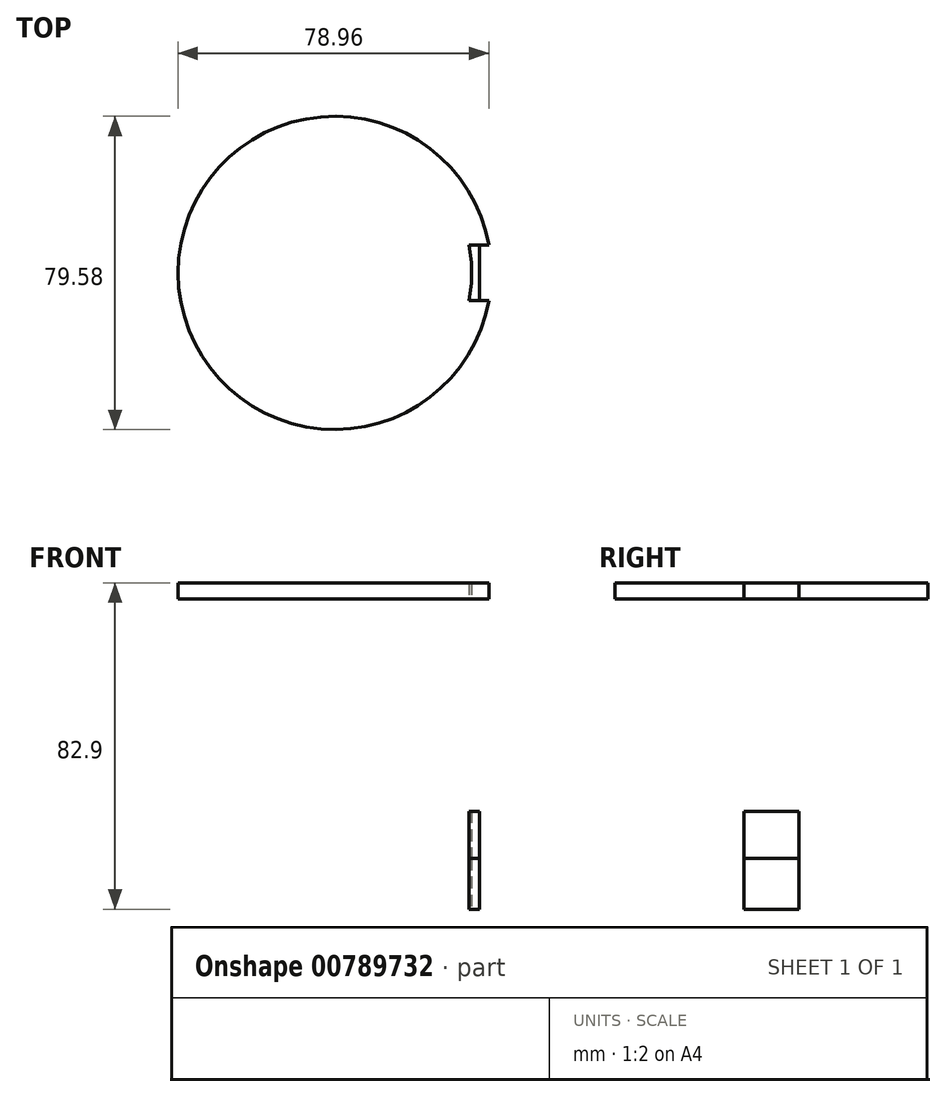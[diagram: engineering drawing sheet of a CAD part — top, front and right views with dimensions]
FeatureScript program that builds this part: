
annotation { "Feature Type Name" : "Feature", "Feature Type Description" : "" }
export const myFeature = defineFeature(function(context is Context, id is Id, definition is map)
    precondition{}
    {
        {
            var Q0;
            Q0=qCreatedBy(makeId("Top.planeOp"),FACE);
            var sketch = newSketch(context, id + "F0", { "sketchPlane" : qUnion([Q0])});
            skCircle(sketch, "E0", {"center": v(0, 0) * mm, "radius": 39.79 * mm});
            skCircle(sketch, "E1", {"center": v(0, 0) * mm, "radius": 34.79 * mm});
            skLineSegment(sketch, "E2.bottom", {"start": v(21, 7) * mm, "end": v(25, 7) * mm});
            skLineSegment(sketch, "E2.top", {"start": v(21, 4) * mm, "end": v(25, 4) * mm});
            skLineSegment(sketch, "E2.left", {"start": v(21, 7) * mm, "end": v(21, 4) * mm});
            skLineSegment(sketch, "E2.right", {"start": v(25, 7) * mm, "end": v(25, 4) * mm});
            skLineSegment(sketch, "E3.MirrorCS", {"start": v(25, -7) * mm, "end": v(25, -4) * mm});
            skLineSegment(sketch, "E4.MirrorCS", {"start": v(21, -4) * mm, "end": v(25, -4) * mm});
            skLineSegment(sketch, "E5.MirrorCS", {"start": v(21, -7) * mm, "end": v(25, -7) * mm});
            skLineSegment(sketch, "E6.MirrorCS", {"start": v(21, -7) * mm, "end": v(21, -4) * mm});
            skLineSegment(sketch, "E7.bottom", {"start": v(21, 7) * mm, "end": v(39.47, 7) * mm});
            skLineSegment(sketch, "E7.top", {"start": v(21, 5) * mm, "end": v(39.47, 5) * mm});
            skLineSegment(sketch, "E7.left", {"start": v(21, 7) * mm, "end": v(21, 5) * mm});
            skLineSegment(sketch, "E7.right", {"start": v(39.47, 7) * mm, "end": v(39.47, 5) * mm});
            skLineSegment(sketch, "E8.bottom", {"start": v(21, -4) * mm, "end": v(39.47, -4) * mm});
            skLineSegment(sketch, "E8.top", {"start": v(21, -7) * mm, "end": v(39.47, -7) * mm});
            skLineSegment(sketch, "E8.left", {"start": v(21, -4) * mm, "end": v(21, -7) * mm});
            skLineSegment(sketch, "E8.right", {"start": v(39.47, -4) * mm, "end": v(39.47, -7) * mm});
            skLineSegment(sketch, "E9.left", {"start": v(21, 7) * mm, "end": v(21, -7) * mm});
            skLineSegment(sketch, "E9.right", {"start": v(25, 7) * mm, "end": v(25, -7) * mm});
            skSolve(sketch);
        }
        {
            var Q0;
            {var subQ3=sQuery(id+"F0.wireOp",EDGE,"E7.bottom");var subQ5=sQuery(id+"F0.wireOp",EDGE,"E1");var subQ6=makeQuery(id+"F0.imprint","INTERSECT",VERTEX,{"derivedFrom":[subQ5,subQ3]});Q0=makeQuery(id+"F0.imprint","IMPRINT",FACE,{"disambiguationData":[TD([[makeQuery(id+"F0.imprint","IMPRINT",EDGE,{"disambiguationData":[TD([[subQ6,1.0]])],"derivedFrom":subQ5}),-1.0]])]});}
            var Q1;
            {var subQ0=sQuery(id+"F0.wireOp",EDGE,"E7.top");var subQ5=sQuery(id+"F0.wireOp",EDGE,"E1");var subQ6=makeQuery(id+"F0.imprint","INTERSECT",VERTEX,{"derivedFrom":[subQ5,subQ0]});Q1=makeQuery(id+"F0.imprint","IMPRINT",FACE,{"disambiguationData":[TD([[makeQuery(id+"F0.imprint","IMPRINT",EDGE,{"disambiguationData":[TD([[subQ6,1.0]])],"derivedFrom":subQ5}),-1.0]])]});}
            var Q2;
            {var subQ3=sQuery(id+"F0.wireOp",EDGE,"E8.top");var subQ5=sQuery(id+"F0.wireOp",EDGE,"E1");var subQ6=makeQuery(id+"F0.imprint","INTERSECT",VERTEX,{"derivedFrom":[subQ5,subQ3]});Q2=makeQuery(id+"F0.imprint","IMPRINT",FACE,{"disambiguationData":[TD([[makeQuery(id+"F0.imprint","IMPRINT",EDGE,{"disambiguationData":[TD([[subQ6,-1.0]])],"derivedFrom":subQ5}),-1.0]])]});}
            extrude(context, id + "F1", {"entities" : qUnion([Q0, Q1, Q2]), "depth" : 160 * mm, "offsetDistance" : 25 * mm, "hasSecondDirection" : true, "secondDirectionOppositeDirection" : false, "secondDirectionDepth" : 90 * mm});
        }
        {
            var Q0;
            Q0=qCreatedBy(makeId("Top.planeOp"),FACE);
            var sketch = newSketch(context, id + "F2", { "sketchPlane" : qUnion([Q0])});
            skLineSegment(sketch, "E10.bottom", {"start": v(33.13, 9) * mm, "end": v(36.74, 9) * mm});
            skLineSegment(sketch, "E10.top", {"start": v(33.13, -11.23) * mm, "end": v(36.74, -11.23) * mm});
            skLineSegment(sketch, "E10.left", {"start": v(33.13, 9) * mm, "end": v(33.13, -11.23) * mm});
            skLineSegment(sketch, "E10.right", {"start": v(36.74, 9) * mm, "end": v(36.74, -11.23) * mm});
            skSolve(sketch);
        }
        {
            var Q0;
            {var subQ0=sQuery(id+"F0.wireOp",EDGE,"E8.top");var subQ1=sQuery(id+"F0.wireOp",EDGE,"E0");var subQ2=makeQuery(id+"F0.imprint","INTERSECT",VERTEX,{"derivedFrom":[subQ1,subQ0]});Q0=makeQuery(id+"F0.imprint","IMPRINT",FACE,{"disambiguationData":[TD([[makeQuery(id+"F0.imprint","IMPRINT",EDGE,{"disambiguationData":[TD([[subQ2,-1.0]])],"derivedFrom":subQ1}),1.0]])]});}
            var Q1;
            {var subQ0=sQuery(id+"F0.wireOp",EDGE,"E7.top");var subQ3=sQuery(id+"F0.wireOp",EDGE,"E1");var subQ4=makeQuery(id+"F0.imprint","INTERSECT",VERTEX,{"derivedFrom":[subQ3,subQ0]});Q1=makeQuery(id+"F0.imprint","IMPRINT",FACE,{"disambiguationData":[TD([[makeQuery(id+"F0.imprint","IMPRINT",EDGE,{"disambiguationData":[TD([[subQ4,1.0]])],"derivedFrom":subQ3}),-1.0]])]});}
            var Q2;
            {var subQ3=sQuery(id+"F0.wireOp",EDGE,"E7.bottom");var subQ5=sQuery(id+"F0.wireOp",EDGE,"E1");var subQ6=makeQuery(id+"F0.imprint","INTERSECT",VERTEX,{"derivedFrom":[subQ5,subQ3]});Q2=makeQuery(id+"F0.imprint","IMPRINT",FACE,{"disambiguationData":[TD([[makeQuery(id+"F0.imprint","IMPRINT",EDGE,{"disambiguationData":[TD([[subQ6,1.0]])],"derivedFrom":subQ5}),-1.0]])]});}
            extrude(context, id + "F3", {"entities" : qUnion([Q0, Q1, Q2]), "depth" : 90 * mm, "offsetDistance" : 25 * mm});
        }
        {
            var Q0;
            Q0=qSketchRegion(id+"F2",true);
            extrude(context, id + "F4", {"entities" : qUnion([Q0]), "operationType" : NewBodyOperationType.INTERSECT, "depth" : 102 * mm, "offsetDistance" : 25 * mm, "hasSecondDirection" : true, "secondDirectionOppositeDirection" : false, "secondDirectionDepth" : 77.1 * mm});
        }
        {
            var Q0;
            {var subQ0=sQuery(id+"F0.wireOp",EDGE,"E7.bottom");var subQ1=sQuery(id+"F0.wireOp",EDGE,"E0");var subQ2=makeQuery(id+"F0.imprint","INTERSECT",VERTEX,{"derivedFrom":[subQ1,subQ0]});Q0=makeQuery(id+"F0.imprint","IMPRINT",FACE,{"disambiguationData":[TD([[makeQuery(id+"F0.imprint","IMPRINT",EDGE,{"disambiguationData":[TD([[subQ2,-1.0]])],"derivedFrom":subQ1}),1.0]])]});}
            var Q1;
            {var subQ0=sQuery(id+"F0.wireOp",EDGE,"E2.bottom");Q1=makeQuery(id+"F0.imprint","IMPRINT",FACE,{"disambiguationData":[TD([[makeQuery(id+"F0.imprint","IMPRINT",EDGE,{"derivedFrom":subQ0}),1.0]])]});}
            var Q2;
            {var subQ2=sQuery(id+"F0.wireOp",EDGE,"E7.top");var subQ4=sQuery(id+"F0.wireOp",EDGE,"E1");var subQ5=makeQuery(id+"F0.imprint","INTERSECT",VERTEX,{"derivedFrom":[subQ4,subQ2]});Q2=makeQuery(id+"F0.imprint","IMPRINT",FACE,{"disambiguationData":[TD([[makeQuery(id+"F0.imprint","IMPRINT",EDGE,{"disambiguationData":[TD([[subQ5,1.0]])],"derivedFrom":subQ4}),1.0]])]});}
            var Q3;
            {var subQ0=sQuery(id+"F0.wireOp",EDGE,"E2.top");Q3=makeQuery(id+"F0.imprint","IMPRINT",FACE,{"disambiguationData":[TD([[makeQuery(id+"F0.imprint","IMPRINT",EDGE,{"derivedFrom":subQ0}),-1.0]])]});}
            var Q4;
            {var subQ0=sQuery(id+"F0.wireOp",EDGE,"E2.top");Q4=makeQuery(id+"F0.imprint","IMPRINT",FACE,{"disambiguationData":[TD([[makeQuery(id+"F0.imprint","IMPRINT",EDGE,{"derivedFrom":subQ0}),1.0]])]});}
            var Q5;
            {var subQ0=sQuery(id+"F0.wireOp",EDGE,"E7.bottom");var subQ1=sQuery(id+"F0.wireOp",EDGE,"E1");var subQ2=makeQuery(id+"F0.imprint","INTERSECT",VERTEX,{"derivedFrom":[subQ1,subQ0]});Q5=makeQuery(id+"F0.imprint","IMPRINT",FACE,{"disambiguationData":[TD([[makeQuery(id+"F0.imprint","IMPRINT",EDGE,{"disambiguationData":[TD([[subQ2,1.0]])],"derivedFrom":subQ1}),1.0]])]});}
            var Q6;
            {var subQ0=sQuery(id+"F0.wireOp",EDGE,"E8.top");var subQ1=sQuery(id+"F0.wireOp",EDGE,"E1");var subQ2=makeQuery(id+"F0.imprint","INTERSECT",VERTEX,{"derivedFrom":[subQ1,subQ0]});Q6=makeQuery(id+"F0.imprint","IMPRINT",FACE,{"disambiguationData":[TD([[makeQuery(id+"F0.imprint","IMPRINT",EDGE,{"disambiguationData":[TD([[subQ2,-1.0]])],"derivedFrom":subQ1}),1.0]])]});}
            var Q7;
            {var subQ5=sQuery(id+"F0.wireOp",EDGE,"E5.MirrorCS");Q7=makeQuery(id+"F0.imprint","IMPRINT",FACE,{"disambiguationData":[TD([[makeQuery(id+"F0.imprint","IMPRINT",EDGE,{"derivedFrom":subQ5}),1.0]])]});}
            var Q8;
            {var subQ5=sQuery(id+"F0.wireOp",EDGE,"E2.bottom");Q8=makeQuery(id+"F0.imprint","IMPRINT",FACE,{"disambiguationData":[TD([[makeQuery(id+"F0.imprint","IMPRINT",EDGE,{"derivedFrom":subQ5}),-1.0]])]});}
            extrude(context, id + "F5", {"entities" : qUnion([Q0, Q1, Q2, Q3, Q4, Q5, Q6, Q7, Q8]), "operationType" : NewBodyOperationType.ADD, "depth" : 160 * mm, "offsetDistance" : 25 * mm, "hasSecondDirection" : true, "secondDirectionOppositeDirection" : true, "secondDirectionDepth" : -156 * mm});
        }
    });
